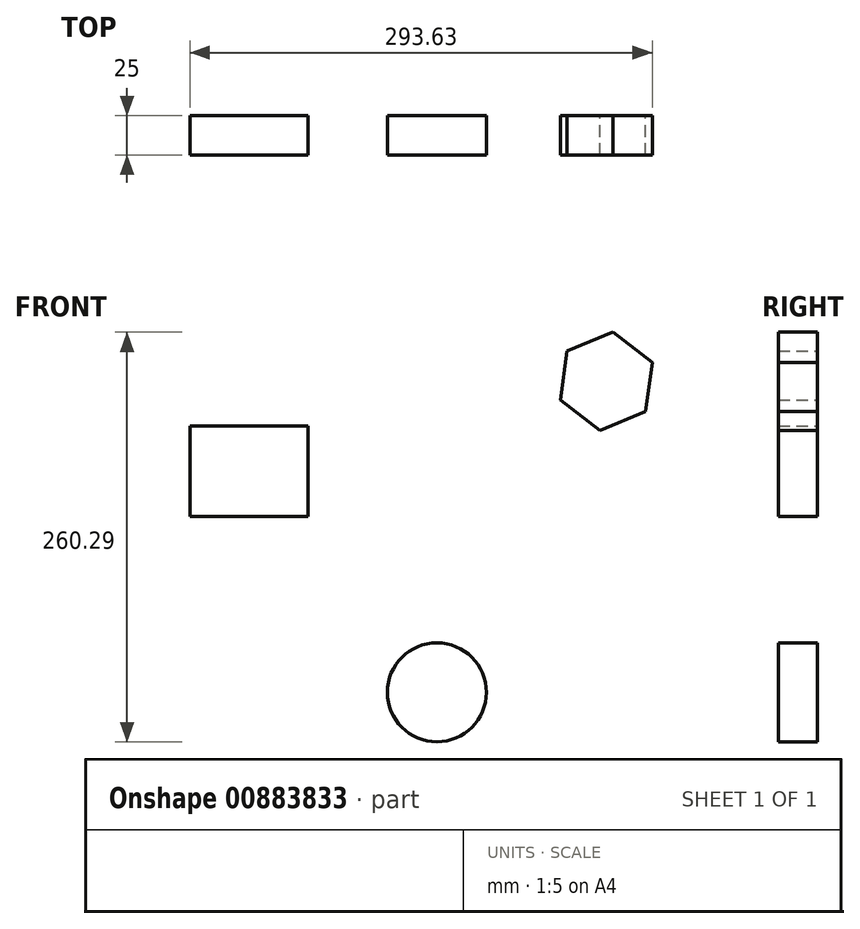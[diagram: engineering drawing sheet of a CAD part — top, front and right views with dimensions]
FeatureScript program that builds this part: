
annotation { "Feature Type Name" : "Feature", "Feature Type Description" : "" }
export const myFeature = defineFeature(function(context is Context, id is Id, definition is map)
    precondition{}
    {
        {
            var Q0;
            Q0=qCreatedBy(makeId("Front.planeOp"),FACE);
            var sketch = newSketch(context, id + "F0", { "sketchPlane" : qUnion([Q0])});
            skLineSegment(sketch, "E0.bottom", {"start": v(-136.66, 41.74) * mm, "end": v(-61.69, 41.74) * mm});
            skLineSegment(sketch, "E0.top", {"start": v(-136.66, -15.62) * mm, "end": v(-61.69, -15.62) * mm});
            skLineSegment(sketch, "E0.left", {"start": v(-136.66, 41.74) * mm, "end": v(-136.66, -15.62) * mm});
            skLineSegment(sketch, "E0.right", {"start": v(-61.69, 41.74) * mm, "end": v(-61.69, -15.62) * mm});
            skSolve(sketch);
        }
        {
            var Q0;
            Q0 = qSketchRegion(id + "F0", true);
            extrude(context, id + "F1", {"entities" : qUnion([Q0]), "depth" : 25 * mm, "offsetDistance" : 25 * mm});
        }
        {
            var Q0;
            Q0=qCreatedBy(makeId("Front.planeOp"),FACE);
            var sketch = newSketch(context, id + "F2", { "sketchPlane" : qUnion([Q0])});
            skCircle(sketch, "E1", {"center": v(20.22, -127.38) * mm, "radius": 31.47 * mm});
            skSolve(sketch);
        }
        {
            var Q0;
            Q0 = qSketchRegion(id + "F2", true);
            extrude(context, id + "F3", {"entities" : qUnion([Q0]), "depth" : 25 * mm, "offsetDistance" : 25 * mm});
        }
        {
            var Q0;
            Q0=qCreatedBy(makeId("Front.planeOp"),FACE);
            var sketch = newSketch(context, id + "F4", { "sketchPlane" : qUnion([Q0])});
            skCircle(sketch, "E2.cCircle", {"center": v(127.86, 70.22) * mm, "radius": 27.28 * mm, "construction": true});
            skLineSegment(sketch, "E2.0", {"start": v(102.9, 89.42) * mm, "end": v(132, 101.44) * mm});
            skLineSegment(sketch, "E2.1", {"start": v(132, 101.44) * mm, "end": v(156.97, 82.24) * mm});
            skLineSegment(sketch, "E2.2", {"start": v(156.97, 82.24) * mm, "end": v(152.82, 51.02) * mm});
            skLineSegment(sketch, "E2.3", {"start": v(152.82, 51.02) * mm, "end": v(123.71, 39) * mm});
            skLineSegment(sketch, "E2.4", {"start": v(123.71, 39) * mm, "end": v(98.75, 58.2) * mm});
            skLineSegment(sketch, "E2.5", {"start": v(98.75, 58.2) * mm, "end": v(102.9, 89.42) * mm});
            skPoint(sketch, "E2.0.midPoint", {"position": v(117.45, 95.43) * mm});
            skSolve(sketch);
        }
        {
            var Q0;
            Q0 = qSketchRegion(id + "F4", true);
            extrude(context, id + "F5", {"entities" : qUnion([Q0]), "depth" : 25 * mm, "offsetDistance" : 25 * mm});
        }
    });
